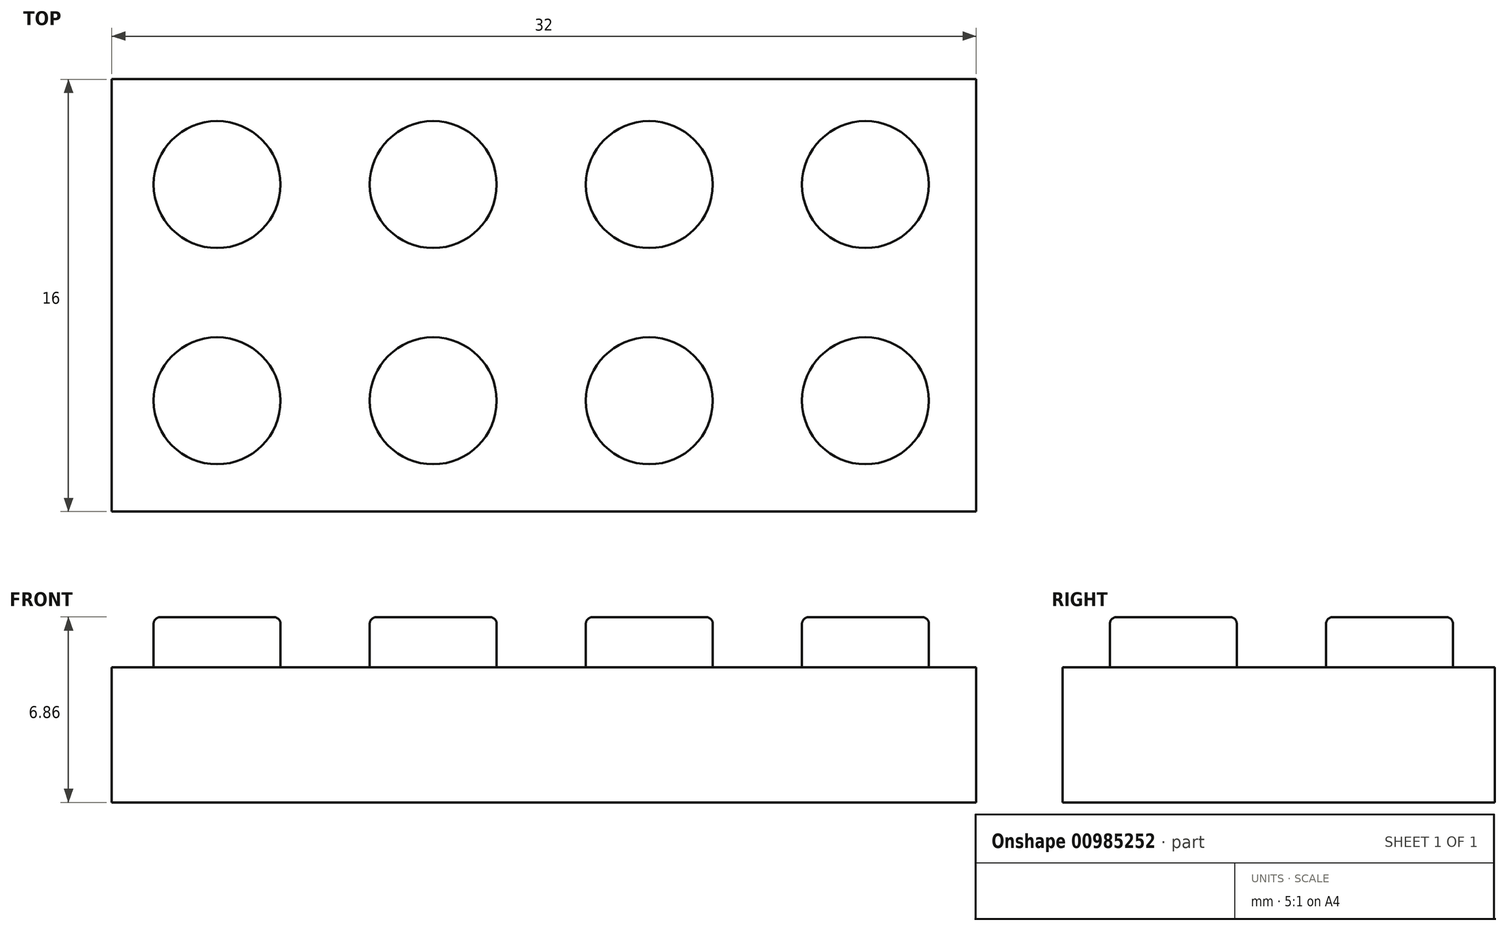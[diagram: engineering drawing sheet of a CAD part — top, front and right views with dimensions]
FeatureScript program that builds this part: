
annotation { "Feature Type Name" : "Feature", "Feature Type Description" : "" }
export const myFeature = defineFeature(function(context is Context, id is Id, definition is map)
    precondition{}
    {
        {
            var Q0;
            Q0=qCreatedBy(makeId("Top.planeOp"),FACE);
            var sketch = newSketch(context, id + "F0", { "sketchPlane" : qUnion([Q0])});
            skLineSegment(sketch, "E0.bottom", {"start": v(0, 0) * mm, "end": v(32, 0) * mm});
            skLineSegment(sketch, "E0.top", {"start": v(0, 16) * mm, "end": v(32, 16) * mm});
            skLineSegment(sketch, "E0.left", {"start": v(0, 0) * mm, "end": v(0, 16) * mm});
            skLineSegment(sketch, "E0.right", {"start": v(32, 0) * mm, "end": v(32, 16) * mm});
            skSolve(sketch);
        }
        {
            var Q0;
            Q0 = qSketchRegion(id + "F0", true);
            extrude(context, id + "F1", {"entities" : qUnion([Q0]), "depth" : 5 * mm, "offsetDistance" : 25.4 * mm});
        }
        {
            var Q0;
            Q0=makeQuery(id+"F1.opExtrude","CAP_FACE",FACE,{"disambiguationData":[OSD([sQuery(id+"F0.wireOp",EDGE,"E0.bottom"),sQuery(id+"F0.wireOp",EDGE,"E0.top"),sQuery(id+"F0.wireOp",EDGE,"E0.left"),sQuery(id+"F0.wireOp",EDGE,"E0.right")])],"isStart":false});
            var sketch = newSketch(context, id + "F2", { "sketchPlane" : qUnion([Q0])});
            skCircle(sketch, "E1", {"center": v(3.9, 12.1) * mm, "radius": 2.35 * mm});
            skCircle(sketch, "E2.0.1.0", {"center": v(3.9, 4.1) * mm, "radius": 2.35 * mm});
            skCircle(sketch, "E2.1.0.0", {"center": v(11.9, 12.1) * mm, "radius": 2.35 * mm});
            skCircle(sketch, "E2.1.1.0", {"center": v(11.9, 4.1) * mm, "radius": 2.35 * mm});
            skCircle(sketch, "E2.2.0.0", {"center": v(19.9, 12.1) * mm, "radius": 2.35 * mm});
            skCircle(sketch, "E2.2.1.0", {"center": v(19.9, 4.1) * mm, "radius": 2.35 * mm});
            skCircle(sketch, "E2.3.0.0", {"center": v(27.9, 12.1) * mm, "radius": 2.35 * mm});
            skCircle(sketch, "E2.3.1.0", {"center": v(27.9, 4.1) * mm, "radius": 2.35 * mm});
            skLineSegment(sketch, "E2.direction1", {"start": v(3.9, 12.1) * mm, "end": v(11.9, 12.1) * mm, "construction": true});
            skLineSegment(sketch, "E2.direction2", {"start": v(3.9, 12.1) * mm, "end": v(3.9, 4.1) * mm, "construction": true});
            skSolve(sketch);
        }
        {
            var Q0;
            Q0=makeQuery(id+"F2.imprint","IMPRINT",FACE,{"disambiguationData":[TD([[makeQuery(id+"F2.imprint","IMPRINT",EDGE,{"derivedFrom":sQuery(id+"F2.wireOp",EDGE,"E1")}),1.0]])]});
            var Q1;
            Q1=makeQuery(id+"F2.imprint","IMPRINT",FACE,{"disambiguationData":[TD([[makeQuery(id+"F2.imprint","IMPRINT",EDGE,{"derivedFrom":sQuery(id+"F2.wireOp",EDGE,"E2.1.0.0")}),1.0]])]});
            var Q2;
            Q2=makeQuery(id+"F2.imprint","IMPRINT",FACE,{"disambiguationData":[TD([[makeQuery(id+"F2.imprint","IMPRINT",EDGE,{"derivedFrom":sQuery(id+"F2.wireOp",EDGE,"E2.2.0.0")}),1.0]])]});
            var Q3;
            Q3=makeQuery(id+"F2.imprint","IMPRINT",FACE,{"disambiguationData":[TD([[makeQuery(id+"F2.imprint","IMPRINT",EDGE,{"derivedFrom":sQuery(id+"F2.wireOp",EDGE,"E2.3.0.0")}),1.0]])]});
            var Q4;
            Q4=makeQuery(id+"F2.imprint","IMPRINT",FACE,{"disambiguationData":[TD([[makeQuery(id+"F2.imprint","IMPRINT",EDGE,{"derivedFrom":sQuery(id+"F2.wireOp",EDGE,"E2.0.1.0")}),1.0]])]});
            var Q5;
            Q5=makeQuery(id+"F2.imprint","IMPRINT",FACE,{"disambiguationData":[TD([[makeQuery(id+"F2.imprint","IMPRINT",EDGE,{"derivedFrom":sQuery(id+"F2.wireOp",EDGE,"E2.1.1.0")}),1.0]])]});
            var Q6;
            Q6=makeQuery(id+"F2.imprint","IMPRINT",FACE,{"disambiguationData":[TD([[makeQuery(id+"F2.imprint","IMPRINT",EDGE,{"derivedFrom":sQuery(id+"F2.wireOp",EDGE,"E2.2.1.0")}),1.0]])]});
            var Q7;
            Q7=makeQuery(id+"F2.imprint","IMPRINT",FACE,{"disambiguationData":[TD([[makeQuery(id+"F2.imprint","IMPRINT",EDGE,{"derivedFrom":sQuery(id+"F2.wireOp",EDGE,"E2.3.1.0")}),1.0]])]});
            extrude(context, id + "F3", {"entities" : qUnion([Q0, Q1, Q2, Q3, Q4, Q5, Q6, Q7]), "operationType" : NewBodyOperationType.ADD, "depth" : 1.85 * mm, "offsetDistance" : 25.4 * mm});
        }
        {
            var Q0;
            Q0=makeQuery(id+"F3.opExtrude","CAP_EDGE",EDGE,{"disambiguationData":[OSD([sQuery(id+"F2.wireOp",EDGE,"E2.0.1.0")])],"isStart":false});
            var Q1;
            Q1=makeQuery(id+"F3.opExtrude","CAP_EDGE",EDGE,{"disambiguationData":[OSD([sQuery(id+"F2.wireOp",EDGE,"E1")])],"isStart":false});
            var Q2;
            Q2=makeQuery(id+"F3.opExtrude","CAP_EDGE",EDGE,{"disambiguationData":[OSD([sQuery(id+"F2.wireOp",EDGE,"E2.1.0.0")])],"isStart":false});
            var Q3;
            Q3=makeQuery(id+"F3.opExtrude","CAP_EDGE",EDGE,{"disambiguationData":[OSD([sQuery(id+"F2.wireOp",EDGE,"E2.1.1.0")])],"isStart":false});
            var Q4;
            Q4=makeQuery(id+"F3.opExtrude","CAP_EDGE",EDGE,{"disambiguationData":[OSD([sQuery(id+"F2.wireOp",EDGE,"E2.2.1.0")])],"isStart":false});
            var Q5;
            Q5=makeQuery(id+"F3.opExtrude","CAP_EDGE",EDGE,{"disambiguationData":[OSD([sQuery(id+"F2.wireOp",EDGE,"E2.2.0.0")])],"isStart":false});
            var Q6;
            Q6=makeQuery(id+"F3.opExtrude","CAP_EDGE",EDGE,{"disambiguationData":[OSD([sQuery(id+"F2.wireOp",EDGE,"E2.3.0.0")])],"isStart":false});
            var Q7;
            Q7=makeQuery(id+"F3.opExtrude","CAP_EDGE",EDGE,{"disambiguationData":[OSD([sQuery(id+"F2.wireOp",EDGE,"E2.3.1.0")])],"isStart":false});
            fillet(context, id + "F4", {"entities" : qUnion([Q0, Q1, Q2, Q3, Q4, Q5, Q6, Q7]), "radius" : 0.25 * mm, "tangentPropagation" : true, "allowEdgeOverflow" : false});
        }
    });
